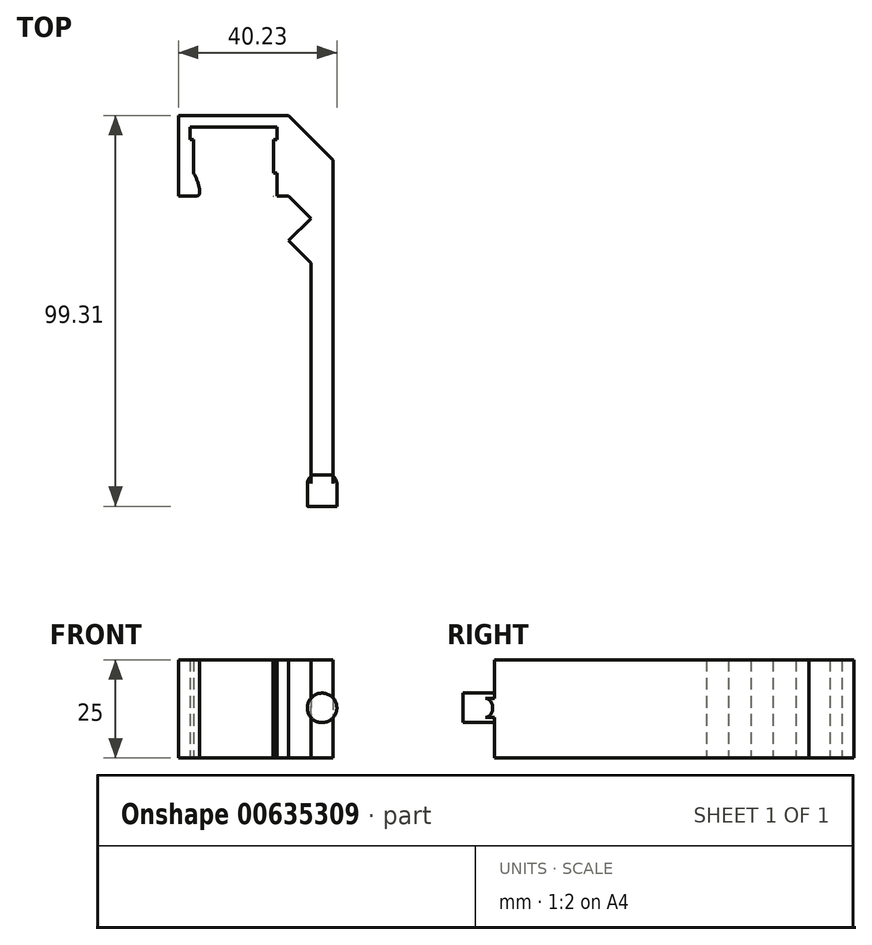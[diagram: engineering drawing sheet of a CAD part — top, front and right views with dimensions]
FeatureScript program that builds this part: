
annotation { "Feature Type Name" : "Feature", "Feature Type Description" : "" }
export const myFeature = defineFeature(function(context is Context, id is Id, definition is map)
    precondition{}
    {
        {
            var Q0;
            Q0=qCreatedBy(makeId("Top.planeOp"),FACE);
            var sketch = newSketch(context, id + "F0", { "sketchPlane" : qUnion([Q0])});
            skLineSegment(sketch, "E0.bottom", {"start": v(-36.31, 27.13) * mm, "end": v(-14.31, 27.13) * mm});
            skLineSegment(sketch, "E0.top", {"start": v(-36.31, 9.63) * mm, "end": v(-14.31, 9.63) * mm});
            skLineSegment(sketch, "E0.left", {"start": v(-36.31, 27.13) * mm, "end": v(-36.31, 9.63) * mm});
            skLineSegment(sketch, "E0.right", {"start": v(-14.31, 27.13) * mm, "end": v(-14.31, 9.63) * mm});
            skLineSegment(sketch, "E1", {"start": v(-36.31, 24.03) * mm, "end": v(-14.31, 24.03) * mm});
            skLineSegment(sketch, "E2", {"start": v(-36.31, 15.43) * mm, "end": v(-14.31, 15.43) * mm});
            skLineSegment(sketch, "E3", {"start": v(-34.01, 10.15) * mm, "end": v(-16.61, 10.15) * mm});
            skLineSegment(sketch, "E4.bottom", {"start": v(-35.46, 15.43) * mm, "end": v(-15.16, 15.43) * mm});
            skLineSegment(sketch, "E4.top", {"start": v(-35.46, 24.03) * mm, "end": v(-15.16, 24.03) * mm});
            skLineSegment(sketch, "E4.left", {"start": v(-35.46, 15.43) * mm, "end": v(-35.46, 24.03) * mm});
            skLineSegment(sketch, "E4.right", {"start": v(-15.16, 15.43) * mm, "end": v(-15.16, 24.03) * mm});
            skFitSpline(sketch, "E5", {"points": [v(-15.16, 9.63) * mm, v(-16.61, 10.15) * mm, v(-15.16, 15.43) * mm], "startDerivative": vector(-5.62, 0) * mm, "endDerivative": vector(4.33, 6.05) * mm});
            skFitSpline(sketch, "E6", {"points": [v(-35.46, 9.63) * mm, v(-34.01, 10.15) * mm, v(-35.46, 15.43) * mm], "startDerivative": vector(6.75, 0) * mm, "endDerivative": vector(-4.33, 6.05) * mm});
            skLineSegment(sketch, "E7.0", {"start": v(-39.31, 30.13) * mm, "end": v(-39.31, 9.63) * mm});
            skLineSegment(sketch, "E7.1", {"start": v(-39.31, 30.13) * mm, "end": v(-11.31, 30.13) * mm});
            skLineSegment(sketch, "E7.2", {"start": v(-11.31, 30.13) * mm, "end": v(-11.31, 7.92) * mm});
            skLineSegment(sketch, "E8", {"start": v(-39.31, 9.63) * mm, "end": v(-36.31, 9.63) * mm});
            skLineSegment(sketch, "E9", {"start": v(-14.31, 9.63) * mm, "end": v(-11.31, 9.63) * mm});
            skLineSegment(sketch, "E10", {"start": v(-11.31, 30.13) * mm, "end": v(0, 18.82) * mm});
            skLineSegment(sketch, "E11", {"start": v(0, 18.82) * mm, "end": v(0, -61.18) * mm});
            skLineSegment(sketch, "E12", {"start": v(0, -61.18) * mm, "end": v(-11.31, -61.18) * mm});
            skLineSegment(sketch, "E13", {"start": v(-11.31, -61.18) * mm, "end": v(-11.31, 7.92) * mm});
            skLineSegment(sketch, "E14", {"start": v(-11.31, 9.63) * mm, "end": v(0, -1.68) * mm});
            skLineSegment(sketch, "E15", {"start": v(-5.66, 3.98) * mm, "end": v(-11.31, -1.68) * mm});
            skLineSegment(sketch, "E16", {"start": v(-11.31, -1.68) * mm, "end": v(-5.66, -7.34) * mm});
            skLineSegment(sketch, "E17", {"start": v(-5.66, -7.34) * mm, "end": v(-5.66, -61.18) * mm});
            skSolve(sketch);
        }
        {
            var Q0;
            {var subQ7=sQuery(id+"F0.wireOp",EDGE,"E0.bottom");Q0=makeQuery(id+"F0.imprint","IMPRINT",FACE,{"disambiguationData":[TD([[makeQuery(id+"F0.imprint","IMPRINT",EDGE,{"derivedFrom":subQ7}),1.0]])]});}
            var Q1;
            {var subQ0=sQuery(id+"F0.wireOp",EDGE,"E6");var subQ1=sQuery(id+"F0.wireOp",EDGE,"E0.top");var subQ2=makeQuery(id+"F0.imprint","INTERSECT",VERTEX,{"disambiguationData":[OD(0.0)],"derivedFrom":[subQ1,subQ0]});Q1=makeQuery(id+"F0.imprint","IMPRINT",FACE,{"disambiguationData":[TD([[makeQuery(id+"F0.imprint","IMPRINT",EDGE,{"disambiguationData":[TD([[subQ2,-1.0]])],"derivedFrom":subQ0}),1.0]])]});}
            var Q2;
            {var subQ5=sQuery(id+"F0.wireOp",EDGE,"E4.left");Q2=makeQuery(id+"F0.imprint","IMPRINT",FACE,{"disambiguationData":[TD([[makeQuery(id+"F0.imprint","IMPRINT",EDGE,{"derivedFrom":subQ5}),1.0]])]});}
            var Q3;
            {var subQ5=sQuery(id+"F0.wireOp",EDGE,"E4.right");Q3=makeQuery(id+"F0.imprint","IMPRINT",FACE,{"disambiguationData":[TD([[makeQuery(id+"F0.imprint","IMPRINT",EDGE,{"derivedFrom":subQ5}),-1.0]])]});}
            var Q4;
            {var subQ0=sQuery(id+"F0.wireOp",EDGE,"E5");var subQ1=sQuery(id+"F0.wireOp",EDGE,"E0.top");var subQ2=makeQuery(id+"F0.imprint","INTERSECT",VERTEX,{"disambiguationData":[OD(0.0)],"derivedFrom":[subQ1,subQ0]});Q4=makeQuery(id+"F0.imprint","IMPRINT",FACE,{"disambiguationData":[TD([[makeQuery(id+"F0.imprint","IMPRINT",EDGE,{"disambiguationData":[TD([[subQ2,-1.0]])],"derivedFrom":subQ0}),-1.0]])]});}
            var Q5;
            {var subQ4=sQuery(id+"F0.wireOp",EDGE,"E10");Q5=makeQuery(id+"F0.imprint","IMPRINT",FACE,{"disambiguationData":[TD([[makeQuery(id+"F0.imprint","IMPRINT",EDGE,{"derivedFrom":subQ4}),-1.0]])]});}
            var Q6;
            {var subQ0=sQuery(id+"F0.wireOp",EDGE,"E15");Q6=makeQuery(id+"F0.imprint","IMPRINT",FACE,{"disambiguationData":[TD([[makeQuery(id+"F0.imprint","IMPRINT",EDGE,{"derivedFrom":subQ0}),1.0]])]});}
            extrude(context, id + "F1", {"entities" : qUnion([Q0, Q1, Q2, Q3, Q4, Q5, Q6]), "depth" : 25 * mm, "offsetDistance" : 25 * mm});
        }
        {
            var Q0;
            Q0=makeQuery(id+"F1.opExtrude","SWEPT_FACE",FACE,{"disambiguationData":[OSD([sQuery(id+"F0.wireOp",EDGE,"E12")])]});
            var sketch = newSketch(context, id + "F2", { "sketchPlane" : qUnion([Q0])});
            skCircle(sketch, "E18", {"center": v(-2.83, 12.77) * mm, "radius": 3.75 * mm});
            skSolve(sketch);
        }
        {
            var Q0;
            {var subQ0=sQuery(id+"F2.wireOp",EDGE,"E18");var subQ1=makeQuery(id+"F1.opExtrude","SWEPT_EDGE",EDGE,{"disambiguationData":[OSD([sQuery(id+"F0.wireOp",EDGE,"E12"),sQuery(id+"F0.wireOp",EDGE,"E17")])]});var subQ2=makeQuery(id+"F2.imprint","INTERSECT",VERTEX,{"disambiguationData":[OD(0.0)],"derivedFrom":[subQ1,subQ0]});Q0=makeQuery(id+"F2.imprint","IMPRINT",FACE,{"disambiguationData":[TD([[makeQuery(id+"F2.imprint","IMPRINT",EDGE,{"disambiguationData":[TD([[subQ2,-1.0]])],"derivedFrom":subQ0}),1.0]])]});}
            var Q1;
            {var subQ0=sQuery(id+"F2.wireOp",EDGE,"E18");var subQ1=sQuery(id+"F0.wireOp",EDGE,"E12");var subQ2=makeQuery(id+"F1.opExtrude","SWEPT_EDGE",EDGE,{"disambiguationData":[OSD([subQ1,sQuery(id+"F0.wireOp",EDGE,"E17")])]});var subQ3=makeQuery(id+"F2.imprint","INTERSECT",VERTEX,{"disambiguationData":[OD(0.0)],"derivedFrom":[subQ2,subQ0]});Q1=makeQuery(id+"F2.imprint","IMPRINT",FACE,{"disambiguationData":[TD([[makeQuery(id+"F2.imprint","IMPRINT",EDGE,{"disambiguationData":[TD([[subQ3,1.0]])],"derivedFrom":subQ0}),1.0]])]});}
            var Q2;
            {var subQ0=sQuery(id+"F2.wireOp",EDGE,"E18");var subQ1=makeQuery(id+"F1.opExtrude","SWEPT_EDGE",EDGE,{"disambiguationData":[OSD([sQuery(id+"F0.wireOp",EDGE,"E11"),sQuery(id+"F0.wireOp",EDGE,"E12")])]});var subQ2=makeQuery(id+"F2.imprint","INTERSECT",VERTEX,{"disambiguationData":[OD(0.0)],"derivedFrom":[subQ1,subQ0]});Q2=makeQuery(id+"F2.imprint","IMPRINT",FACE,{"disambiguationData":[TD([[makeQuery(id+"F2.imprint","IMPRINT",EDGE,{"disambiguationData":[TD([[subQ2,1.0]])],"derivedFrom":subQ0}),1.0]])]});}
            extrude(context, id + "F3", {"entities" : qUnion([Q0, Q1, Q2]), "operationType" : NewBodyOperationType.ADD, "depth" : 8 * mm, "offsetDistance" : 25 * mm});
        }
        {
            var Q0;
            {var subQ0=sQuery(id+"F2.wireOp",EDGE,"E18");var subQ1=makeQuery(id+"F3.opExtrude","SWEPT_FACE",FACE,{"disambiguationData":[OSD([subQ0])]});var subQ2=makeQuery(id+"F3.opExtrude","CAP_FACE",FACE,{"disambiguationData":[OSD([subQ0])],"isStart":true});Q0=makeQuery(id+"F3.boolean.opBoolean","SPLIT",EDGE,{"disambiguationData":[topologyDisambiguationEdgeConnected([subQ1,subQ2]),TD([makeQuery(id+"F1.opExtrude","SWEPT_FACE",FACE,{"disambiguationData":[OSD([sQuery(id+"F0.wireOp",EDGE,"E11")])]})])],"derivedFrom":makeQuery(id+"F3.opExtrude","CAP_EDGE",EDGE,{"disambiguationData":[OSD([subQ0])],"isStart":true})});}
            var Q1;
            {var subQ0=sQuery(id+"F2.wireOp",EDGE,"E18");var subQ1=makeQuery(id+"F3.opExtrude","SWEPT_FACE",FACE,{"disambiguationData":[OSD([subQ0])]});var subQ2=makeQuery(id+"F3.opExtrude","CAP_FACE",FACE,{"disambiguationData":[OSD([subQ0])],"isStart":true});Q1=makeQuery(id+"F3.boolean.opBoolean","SPLIT",EDGE,{"disambiguationData":[topologyDisambiguationEdgeConnected([subQ1,subQ2]),TD([makeQuery(id+"F1.opExtrude","SWEPT_FACE",FACE,{"disambiguationData":[OSD([sQuery(id+"F0.wireOp",EDGE,"E17")])]})])],"derivedFrom":makeQuery(id+"F3.opExtrude","CAP_EDGE",EDGE,{"disambiguationData":[OSD([subQ0])],"isStart":true})});}
            fillet(context, id + "F4", {"entities" : qUnion([Q0, Q1]), "radius" : 2.27 * mm, "tangentPropagation" : true, "allowEdgeOverflow" : false});
        }
    });
